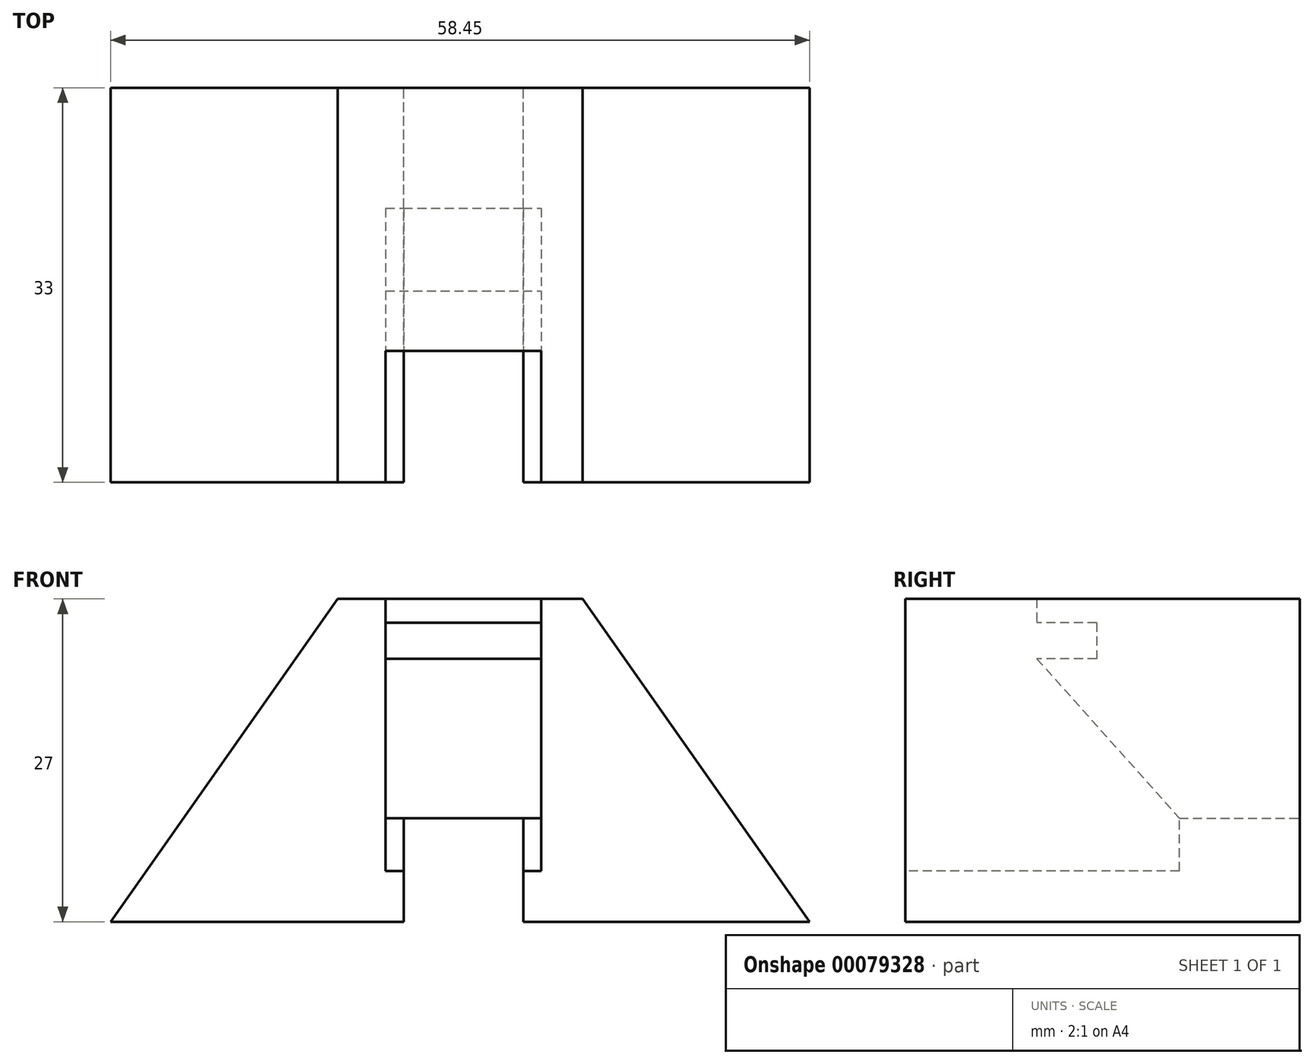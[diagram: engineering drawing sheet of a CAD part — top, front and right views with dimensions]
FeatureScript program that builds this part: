
annotation { "Feature Type Name" : "Feature", "Feature Type Description" : "" }
export const myFeature = defineFeature(function(context is Context, id is Id, definition is map)
    precondition{}
    {
        {
            var Q0;
            Q0=qCreatedBy(makeId("Front.planeOp"),FACE);
            var sketch = newSketch(context, id + "F0", { "sketchPlane" : qUnion([Q0])});
            skLineSegment(sketch, "E0", {"start": v(-29.5, 0) * mm, "end": v(-5, 0) * mm});
            skLineSegment(sketch, "E1", {"start": v(28.95, 0) * mm, "end": v(9.97, 27) * mm});
            skLineSegment(sketch, "E2", {"start": v(9.97, 27) * mm, "end": v(-10.53, 27) * mm});
            skLineSegment(sketch, "E3", {"start": v(-10.53, 27) * mm, "end": v(-29.5, 0) * mm});
            skLineSegment(sketch, "E4.top", {"start": v(-5, 8.67) * mm, "end": v(5, 8.67) * mm});
            skLineSegment(sketch, "E4.left", {"start": v(-5, 0) * mm, "end": v(-5, 8.67) * mm});
            skLineSegment(sketch, "E4.right", {"start": v(5, 0) * mm, "end": v(5, 8.67) * mm});
            skLineSegment(sketch, "E5.trimOffspring", {"start": v(5, 0) * mm, "end": v(28.95, 0) * mm});
            skSolve(sketch);
        }
        {
            var Q0;
            Q0 = qSketchRegion(id + "F0", true);
            extrude(context, id + "F1", {"entities" : qUnion([Q0]), "depth" : 33 * mm});
        }
        {
            var Q0;
            Q0=makeQuery(id+"F1.opExtrude","CAP_FACE",FACE,{"disambiguationData":[OSD([sQuery(id+"F0.wireOp",EDGE,"E0"),sQuery(id+"F0.wireOp",EDGE,"E1"),sQuery(id+"F0.wireOp",EDGE,"E2"),sQuery(id+"F0.wireOp",EDGE,"E3"),sQuery(id+"F0.wireOp",EDGE,"E4.top"),sQuery(id+"F0.wireOp",EDGE,"E4.left"),sQuery(id+"F0.wireOp",EDGE,"E4.right"),sQuery(id+"F0.wireOp",EDGE,"E5.trimOffspring")])],"isStart":false});
            var sketch = newSketch(context, id + "F2", { "sketchPlane" : qUnion([Q0])});
            skLineSegment(sketch, "E6.bottom", {"start": v(-6.5, 27) * mm, "end": v(6.5, 27) * mm});
            skLineSegment(sketch, "E6.top", {"start": v(-6.5, 4.25) * mm, "end": v(6.5, 4.25) * mm});
            skLineSegment(sketch, "E6.left", {"start": v(-6.5, 27) * mm, "end": v(-6.5, 4.25) * mm});
            skLineSegment(sketch, "E6.right", {"start": v(6.5, 27) * mm, "end": v(6.5, 4.25) * mm});
            skSolve(sketch);
        }
        {
            var Q0;
            Q0 = qSketchRegion(id + "F2", true);
            extrude(context, id + "F3", {"entities" : qUnion([Q0]), "operationType" : NewBodyOperationType.REMOVE, "oppositeDirection" : true, "depth" : 11 * mm});
        }
        {
            var Q0;
            Q0=makeQuery(id+"F3.boolean.opBoolean","COPY",FACE,{"derivedFrom":makeQuery(id+"F3.opExtrude","CAP_FACE",FACE,{"disambiguationData":[OSD([sQuery(id+"F2.wireOp",EDGE,"E6.bottom"),sQuery(id+"F2.wireOp",EDGE,"E6.top"),sQuery(id+"F2.wireOp",EDGE,"E6.left"),sQuery(id+"F2.wireOp",EDGE,"E6.right")])],"isStart":false})});
            var sketch = newSketch(context, id + "F4", { "sketchPlane" : qUnion([Q0])});
            skLineSegment(sketch, "E7.bottom", {"start": v(-6.5, 25) * mm, "end": v(6.5, 25) * mm});
            skLineSegment(sketch, "E7.top", {"start": v(-6.5, 22) * mm, "end": v(6.5, 22) * mm});
            skLineSegment(sketch, "E7.left", {"start": v(-6.5, 25) * mm, "end": v(-6.5, 22) * mm});
            skLineSegment(sketch, "E7.right", {"start": v(6.5, 25) * mm, "end": v(6.5, 22) * mm});
            skSolve(sketch);
        }
        {
            var Q0;
            Q0 = qSketchRegion(id + "F4", true);
            extrude(context, id + "F5", {"entities" : qUnion([Q0]), "operationType" : NewBodyOperationType.REMOVE, "oppositeDirection" : true, "depth" : 5 * mm});
        }
        {
            var Q0;
            Q0=qCreatedBy(makeId("Right.planeOp"),FACE);
            var sketch = newSketch(context, id + "F6", { "sketchPlane" : qUnion([Q0])});
            skLineSegment(sketch, "E8", {"start": v(-22, 22) * mm, "end": v(-10.09, 8.67) * mm});
            skLineSegment(sketch, "E9", {"start": v(-22, 22) * mm, "end": v(-22, 8.67) * mm});
            skLineSegment(sketch, "E10.top", {"start": v(-10.09, 4.25) * mm, "end": v(-22, 4.25) * mm});
            skLineSegment(sketch, "E10.left", {"start": v(-10.09, 8.67) * mm, "end": v(-10.09, 4.25) * mm});
            skLineSegment(sketch, "E10.right", {"start": v(-22, 8.79) * mm, "end": v(-22, 4.25) * mm});
            skSolve(sketch);
        }
        {
            var Q0;
            Q0 = qSketchRegion(id + "F6", true);
            extrude(context, id + "F7", {"entities" : qUnion([Q0]), "operationType" : NewBodyOperationType.REMOVE, "endBound" : BoundingType.SYMMETRIC, "oppositeDirection" : true, "depth" : 13 * mm});
        }
    });
